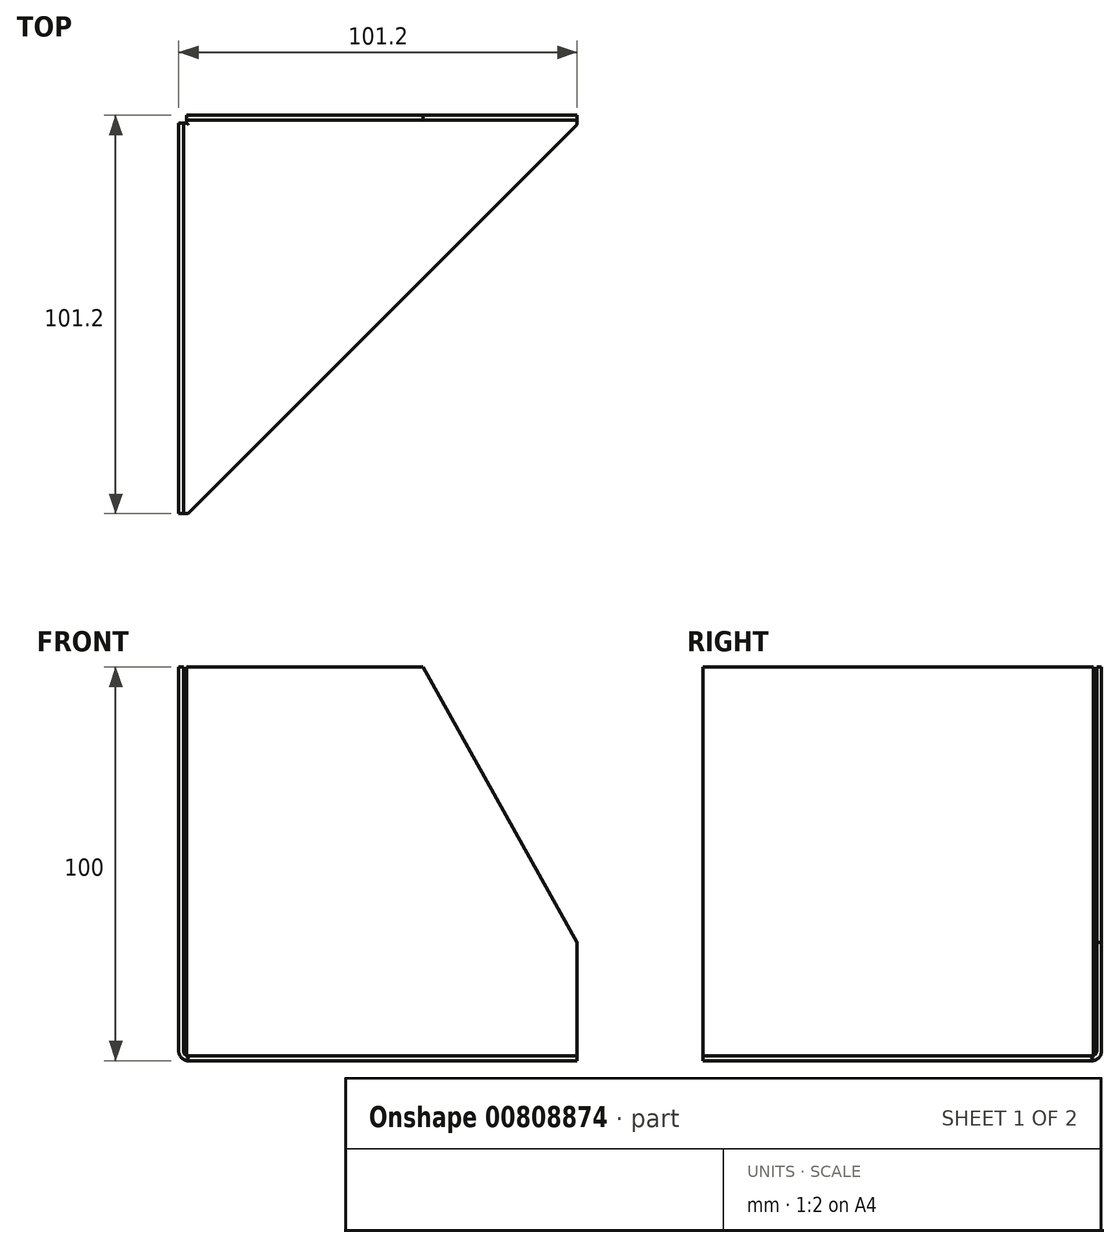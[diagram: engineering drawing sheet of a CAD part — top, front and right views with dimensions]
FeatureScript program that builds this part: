
annotation { "Feature Type Name" : "Feature", "Feature Type Description" : "" }
export const myFeature = defineFeature(function(context is Context, id is Id, definition is map)
    precondition{}
    {
        {
            var Q0;
            Q0=qCreatedBy(makeId("Top.planeOp"),FACE);
            var sketch = newSketch(context, id + "F0", { "sketchPlane" : qUnion([Q0])});
            skLineSegment(sketch, "E0.bottom", {"start": v(50.6, -50.6) * mm, "end": v(-50.6, -50.6) * mm});
            skLineSegment(sketch, "E0.top", {"start": v(50.6, 50.6) * mm, "end": v(-50.6, 50.6) * mm});
            skLineSegment(sketch, "E0.left", {"start": v(50.6, -50.6) * mm, "end": v(50.6, 50.6) * mm});
            skLineSegment(sketch, "E0.right", {"start": v(-50.6, -50.6) * mm, "end": v(-50.6, 50.6) * mm});
            skPoint(sketch, "E0.middle", {"position": v(0, 0) * mm});
            skSolve(sketch);
        }
        {
            var Q0;
            Q0=qSketchRegion(id+"F0",true);
            extrude(context, id + "F1", {"entities" : qUnion([Q0]), "depth" : 100 * mm, "offsetDistance" : 25 * mm});
        }
        {
            var Q0;
            Q0=makeQuery(id+"F1.opExtrude","CAP_FACE",FACE,{"disambiguationData":[OSD([sQuery(id+"F0.wireOp",EDGE,"E0.bottom"),sQuery(id+"F0.wireOp",EDGE,"E0.top"),sQuery(id+"F0.wireOp",EDGE,"E0.left"),sQuery(id+"F0.wireOp",EDGE,"E0.right")])],"isStart":false});
            var Q1;
            Q1=makeQuery(id+"F1.opExtrude","SWEPT_FACE",FACE,{"disambiguationData":[OSD([sQuery(id+"F0.wireOp",EDGE,"E0.bottom")])]});
            var Q2;
            Q2=makeQuery(id+"F1.opExtrude","SWEPT_FACE",FACE,{"disambiguationData":[OSD([sQuery(id+"F0.wireOp",EDGE,"E0.left")])]});
            shell(context, id + "F2", {"entities" : qUnion([Q0, Q1, Q2]), "thickness" : 1.2 * mm});
        }
        {
            var Q0;
            Q0=makeQuery(id+"F1.opExtrude","CAP_FACE",FACE,{"disambiguationData":[OSD([sQuery(id+"F0.wireOp",EDGE,"E0.bottom"),sQuery(id+"F0.wireOp",EDGE,"E0.top"),sQuery(id+"F0.wireOp",EDGE,"E0.left"),sQuery(id+"F0.wireOp",EDGE,"E0.right")])],"isStart":true});
            var sketch = newSketch(context, id + "F3", { "sketchPlane" : qUnion([Q0])});
            skLineSegment(sketch, "E1.bottom", {"start": v(-50.6, -50.6) * mm, "end": v(-49.4, -50.6) * mm});
            skLineSegment(sketch, "E1.top", {"start": v(-50.6, -49.4) * mm, "end": v(-49.4, -49.4) * mm});
            skLineSegment(sketch, "E1.left", {"start": v(-50.6, -50.6) * mm, "end": v(-50.6, -49.4) * mm});
            skLineSegment(sketch, "E1.right", {"start": v(-49.4, -50.6) * mm, "end": v(-49.4, -49.4) * mm});
            skSolve(sketch);
        }
        {
            var Q0;
            Q0=makeQuery(id+"F1.opExtrude","CAP_FACE",FACE,{"disambiguationData":[OSD([sQuery(id+"F0.wireOp",EDGE,"E0.bottom"),sQuery(id+"F0.wireOp",EDGE,"E0.top"),sQuery(id+"F0.wireOp",EDGE,"E0.left"),sQuery(id+"F0.wireOp",EDGE,"E0.right")])],"isStart":false});
            var sketch = newSketch(context, id + "F4", { "sketchPlane" : qUnion([Q0])});
            skLineSegment(sketch, "E2", {"start": v(-50.6, 48.6) * mm, "end": v(-50.6, 50.6) * mm});
            skLineSegment(sketch, "E3", {"start": v(-50.6, 50.6) * mm, "end": v(-48.6, 50.6) * mm});
            skLineSegment(sketch, "E4", {"start": v(-50.6, 48.6) * mm, "end": v(-48.6, 48.6) * mm});
            skLineSegment(sketch, "E5", {"start": v(-48.6, 48.6) * mm, "end": v(-48.6, 50.6) * mm});
            skSolve(sketch);
        }
        {
            var Q0;
            {var subQ0=sQuery(id+"F4.wireOp",EDGE,"E5");var subQ1=sQuery(id+"F4.wireOp",EDGE,"E4");var subQ2=makeQuery(id+"F4.imprint","INTERSECT",VERTEX,{"derivedFrom":[subQ1,subQ0]});Q0=makeQuery(id+"F4.imprint","IMPRINT",FACE,{"disambiguationData":[TD([[makeQuery(id+"F4.imprint","IMPRINT",EDGE,{"disambiguationData":[TD([[subQ2,1.0]])],"derivedFrom":subQ1}),1.0]])]});}
            var Q1;
            {var subQ1=sQuery(id+"F4.wireOp",EDGE,"E2");Q1=makeQuery(id+"F4.imprint","IMPRINT",FACE,{"disambiguationData":[TD([[makeQuery(id+"F4.imprint","IMPRINT",EDGE,{"derivedFrom":subQ1}),-1.0]])]});}
            extrude(context, id + "F5", {"entities" : qUnion([Q0, Q1]), "operationType" : NewBodyOperationType.REMOVE, "endBound" : BoundingType.THROUGH_ALL, "oppositeDirection" : true, "depth" : 25 * mm, "offsetDistance" : 25 * mm});
        }
        {
            var Q0;
            {var subQ0=sQuery(id+"F0.wireOp",EDGE,"E0.top");Q0=makeQuery(id+"F2.opShell","OFFSET_EDGE",EDGE,{"disambiguationData":[OSD([subQ0]),TDD([makeQuery(id+"F1.opExtrude","CAP_EDGE",EDGE,{"disambiguationData":[OSD([subQ0])],"isStart":true})])]});}
            fillet(context, id + "F6", {"entities" : qUnion([Q0]), "radius" : 1.2 * mm, "allowEdgeOverflow" : false});
        }
        {
            var Q0;
            {var subQ0=sQuery(id+"F0.wireOp",EDGE,"E0.right");Q0=makeQuery(id+"F2.opShell","OFFSET_EDGE",EDGE,{"disambiguationData":[OSD([subQ0]),TDD([makeQuery(id+"F1.opExtrude","CAP_EDGE",EDGE,{"disambiguationData":[OSD([subQ0])],"isStart":true})])]});}
            fillet(context, id + "F7", {"entities" : qUnion([Q0]), "radius" : 1.2 * mm, "tangentPropagation" : true, "allowEdgeOverflow" : false});
        }
        {
            var Q0;
            Q0=makeQuery(id+"F1.opExtrude","CAP_EDGE",EDGE,{"disambiguationData":[OSD([sQuery(id+"F0.wireOp",EDGE,"E0.right")])],"isStart":true});
            fillet(context, id + "F8", {"entities" : qUnion([Q0]), "radius" : 2.4 * mm, "tangentPropagation" : true, "allowEdgeOverflow" : false});
        }
        {
            var Q0;
            Q0=makeQuery(id+"F1.opExtrude","CAP_EDGE",EDGE,{"disambiguationData":[OSD([sQuery(id+"F0.wireOp",EDGE,"E0.top")])],"isStart":true});
            fillet(context, id + "F9", {"entities" : qUnion([Q0]), "radius" : 2.4 * mm, "tangentPropagation" : true, "allowEdgeOverflow" : false});
        }
        {
            var Q0;
            Q0=makeQuery(id+"F1.opExtrude","SWEPT_FACE",FACE,{"disambiguationData":[OSD([sQuery(id+"F0.wireOp",EDGE,"E0.right")])]});
            var sketch = newSketch(context, id + "F10", { "sketchPlane" : qUnion([Q0])});
            skLineSegment(sketch, "E6", {"start": v(50.6, 100) * mm, "end": v(50.6, 30) * mm});
            skLineSegment(sketch, "E7", {"start": v(50.6, 30) * mm, "end": v(11.4, 100) * mm});
            skLineSegment(sketch, "E8", {"start": v(11.4, 100) * mm, "end": v(50.6, 100) * mm});
            skSolve(sketch);
        }
        {
            var Q0;
            Q0=makeQuery(id+"F1.opExtrude","SWEPT_FACE",FACE,{"disambiguationData":[OSD([sQuery(id+"F0.wireOp",EDGE,"E0.top")])]});
            var sketch = newSketch(context, id + "F11", { "sketchPlane" : qUnion([Q0])});
            skLineSegment(sketch, "E9", {"start": v(-50.6, 100) * mm, "end": v(-11.4, 100) * mm});
            skLineSegment(sketch, "E10", {"start": v(-11.4, 100) * mm, "end": v(-50.6, 30) * mm});
            skLineSegment(sketch, "E11", {"start": v(-50.6, 30) * mm, "end": v(-50.6, 100) * mm});
            skSolve(sketch);
        }
        {
            var Q0;
            Q0=makeQuery(id+"F11.imprint","IMPRINT",FACE,{"disambiguationData":[TD([[makeQuery(id+"F11.imprint","IMPRINT",EDGE,{"derivedFrom":sQuery(id+"F11.wireOp",EDGE,"E9")}),-1.0]])]});
            extrude(context, id + "F12", {"entities" : qUnion([Q0]), "operationType" : NewBodyOperationType.REMOVE, "oppositeDirection" : true, "depth" : 25 * mm, "offsetDistance" : 25 * mm});
        }
        {
            var Q0;
            {var subQ4=sQuery(id+"F3.wireOp",EDGE,"E1.top");Q0=makeQuery(id+"F3.imprint","IMPRINT",FACE,{"disambiguationData":[TD([[makeQuery(id+"F3.imprint","IMPRINT",EDGE,{"derivedFrom":subQ4}),1.0]])]});}
            var sketch = newSketch(context, id + "F13", { "sketchPlane" : qUnion([Q0])});
            skLineSegment(sketch, "E12.0", {"start": v(50.6, 50.6) * mm, "end": v(-48.2, 50.6) * mm});
            skLineSegment(sketch, "E13.0", {"start": v(50.6, 50.6) * mm, "end": v(50.6, -48.2) * mm});
            skLineSegment(sketch, "E14", {"start": v(-48.2, 50.6) * mm, "end": v(50.6, -48.2) * mm});
            skSolve(sketch);
        }
        {
            var Q0;
            Q0=qSketchRegion(id+"F13",true);
            extrude(context, id + "F14", {"entities" : qUnion([Q0]), "operationType" : NewBodyOperationType.REMOVE, "oppositeDirection" : true, "depth" : 25 * mm, "offsetDistance" : 25 * mm});
        }
    });
